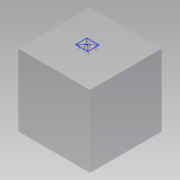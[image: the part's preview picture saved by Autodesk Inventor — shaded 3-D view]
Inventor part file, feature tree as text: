
AUTODESK INVENTOR PART (.ipt)
format: ipt  version: 2014 (Build 180170000, 170)  size: 184,832 bytes
history: native  units: mm
features: other x49, sketch x2, extrude x1
ambient origin geometry x8: Origin, YZ Plane, XZ Plane, XY Plane, X Axis, Y Axis, Z Axis, Center Point
bodies: 实体1 (feature_tree)
feature tree (52):
  extrude  "拉伸1"  TaperAngle=0.0deg  [1 undecoded]
  other  "UCS1"
  other  "UCS2"
  other  "UCS3"
  other  "UCS4"
  other  "UCS5"
  other  "UCS6"
  other  "Footprint1"
  sketch  "草图1"  dims[d0=300.0mm d1=0.0mm]
  other  "UCS1: YZ 平面"
  other  "UCS1: XZ 平面"
  other  "UCS1: XY 平面"
  other  "UCS1: X 轴"
  other  "UCS1: Y 轴"
  other  "UCS1: Z 轴"
  other  "UCS1: 原点"
  other  "UCS2: YZ 平面"
  other  "UCS2: XZ 平面"
  other  "UCS2: XY 平面"
  other  "UCS2: X 轴"
  other  "UCS2: Y 轴"
  other  "UCS2: Z 轴"
  other  "UCS2: 原点"
  other  "UCS3: YZ 平面"
  other  "UCS3: XZ 平面"
  other  "UCS3: XY 平面"
  other  "UCS3: X 轴"
  other  "UCS3: Y 轴"
  other  "UCS3: Z 轴"
  other  "UCS3: 原点"
  other  "UCS4: YZ 平面"
  other  "UCS4: XZ 平面"
  other  "UCS4: XY 平面"
  other  "UCS4: X 轴"
  other  "UCS4: Y 轴"
  other  "UCS4: Z 轴"
  other  "UCS4: 原点"
  other  "UCS5: YZ 平面"
  other  "UCS5: XZ 平面"
  other  "UCS5: XY 平面"
  other  "UCS5: X 轴"
  other  "UCS5: Y 轴"
  other  "UCS5: Z 轴"
  other  "UCS5: 原点"
  other  "UCS6: YZ 平面"
  other  "UCS6: XZ 平面"
  other  "UCS6: XY 平面"
  other  "UCS6: X 轴"
  other  "UCS6: Y 轴"
  other  "UCS6: Z 轴"
  other  "UCS6: 原点"
  sketch  "草图2"  dims[d2=0.0mm d3=0.0mm d4=0.0mm d5=0.0mm d6=0.0mm d7=0.0mm d8=0.0mm d9=0.0mm d10=0.0mm d11=0.0mm d12=0.0mm d13=0.0mm d14=0.0mm d15=0.0mm d16=0.0mm d17=0.0mm d18=0.0mm d19=0.0mm d20=0.0mm d21=0.0mm d22=0.0mm d23=0.0mm d24=0.0mm d25=0.0mm d26=0.0mm d27=0.0mm d28=0.0mm d29=0.0mm d30=0.0mm d31=0.0mm d32=0.0mm d33=0.0mm d34=0.0mm d35=0.0mm d36=0.0mm d37=0.0mm d38=0.0mm]
note: 1 required parameter value undecoded (feature->parameter linkage not recoverable at this tier; creation-order binding heuristic only, values carry confidence <= 0.55)
